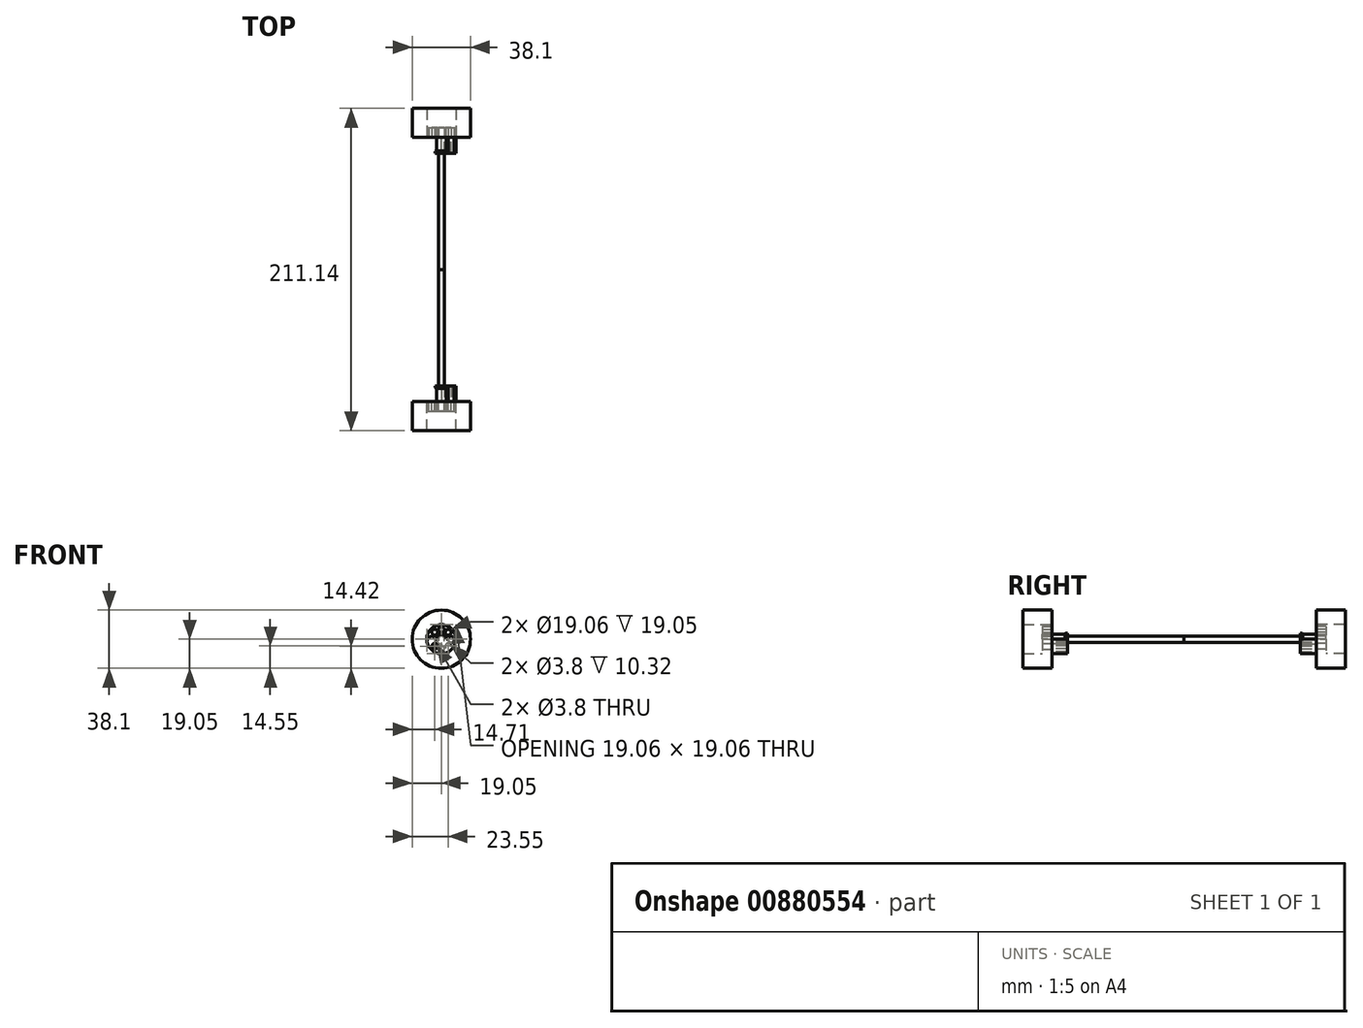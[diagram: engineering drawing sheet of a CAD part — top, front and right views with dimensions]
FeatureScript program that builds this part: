
annotation { "Feature Type Name" : "Feature", "Feature Type Description" : "" }
export const myFeature = defineFeature(function(context is Context, id is Id, definition is map)
    precondition{}
    {
        {
            var Q0;
            Q0=qCreatedBy(makeId("Front.planeOp"),FACE);
            var sketch = newSketch(context, id + "F0", { "sketchPlane" : qUnion([Q0])});
            skCircle(sketch, "E0", {"center": v(0, 0) * mm, "radius": 19.05 * mm});
            skCircle(sketch, "E1", {"center": v(0, 0) * mm, "radius": 9.53 * mm});
            skSolve(sketch);
        }
        {
            var Q0;
            Q0=makeQuery(id+"F0.imprint","IMPRINT",FACE,{"disambiguationData":[TD([[makeQuery(id+"F0.imprint","IMPRINT",EDGE,{"derivedFrom":sQuery(id+"F0.wireOp",EDGE,"E0")}),1.0]])]});
            extrude(context, id + "F1", {"entities" : qUnion([Q0]), "depth" : 19.05 * mm, "offsetDistance" : 25.4 * mm});
        }
        {
            var Q0;
            Q0=makeQuery(id+"F0.imprint","IMPRINT",FACE,{"disambiguationData":[TD([[makeQuery(id+"F0.imprint","IMPRINT",EDGE,{"derivedFrom":sQuery(id+"F0.wireOp",EDGE,"E1")}),1.0]])]});
            extrude(context, id + "F2", {"entities" : qUnion([Q0]), "depth" : 6.35 * mm, "offsetDistance" : 25.4 * mm});
        }
        {
            var Q0;
            Q0=makeQuery(id+"F2.opExtrude","CAP_FACE",FACE,{"disambiguationData":[OSD([sQuery(id+"F0.wireOp",EDGE,"E1")])],"isStart":true});
            var sketch = newSketch(context, id + "F3", { "sketchPlane" : qUnion([Q0])});
            skCircle(sketch, "E2", {"center": v(0, 0) * mm, "radius": 3.18 * mm});
            skLineSegment(sketch, "E3", {"start": v(0, 0) * mm, "end": v(0, 9.53) * mm});
            skLineSegment(sketch, "E4", {"start": v(0, 9.53) * mm, "end": v(0, -9.53) * mm});
            skCircle(sketch, "E5", {"center": v(0, 0) * mm, "radius": 9.53 * mm});
            skLineSegment(sketch, "E6.1.0", {"start": v(9.53, 0) * mm, "end": v(-9.53, 0) * mm});
            skLineSegment(sketch, "E6.2.0", {"start": v(0, -9.53) * mm, "end": v(0, 9.53) * mm});
            skLineSegment(sketch, "E6.anchor1", {"start": v(0, 0) * mm, "end": v(0, -9.53) * mm, "construction": true});
            skLineSegment(sketch, "E6.anchor2", {"start": v(0, 0) * mm, "end": v(0, 9.53) * mm, "construction": true});
            skLineSegment(sketch, "E7", {"start": v(-9.53, 0) * mm, "end": v(-3.18, 0) * mm});
            skCircle(sketch, "E8", {"center": v(-6.35, 0) * mm, "radius": 1.9 * mm});
            skLineSegment(sketch, "E9", {"start": v(0, 0) * mm, "end": v(-6.74, -6.74) * mm});
            skLineSegment(sketch, "E10", {"start": v(-6.74, -6.74) * mm, "end": v(-2.25, -2.25) * mm});
            skCircle(sketch, "E11", {"center": v(-4.5, -4.5) * mm, "radius": 1.9 * mm});
            skLineSegment(sketch, "E12", {"start": v(0, -9.53) * mm, "end": v(0, -3.18) * mm});
            skPoint(sketch, "E12.endSnap0", {"position": v(0, -4.76) * mm});
            skCircle(sketch, "E13", {"center": v(0, -6.35) * mm, "radius": 1.9 * mm});
            skLineSegment(sketch, "E14", {"start": v(2.07, -2.4) * mm, "end": v(6.6, -6.86) * mm});
            skCircle(sketch, "E15", {"center": v(4.34, -4.63) * mm, "radius": 1.9 * mm});
            skLineSegment(sketch, "E16", {"start": v(3.18, 0) * mm, "end": v(9.53, 0) * mm});
            skCircle(sketch, "E17", {"center": v(6.35, 0) * mm, "radius": 1.9 * mm});
            skCircle(sketch, "E18.MirrorC", {"center": v(4.34, 4.63) * mm, "radius": 1.9 * mm});
            skCircle(sketch, "E19.MirrorC", {"center": v(0, 6.35) * mm, "radius": 1.9 * mm});
            skCircle(sketch, "E20.MirrorC", {"center": v(-4.5, 4.5) * mm, "radius": 1.9 * mm});
            skSolve(sketch);
        }
        {
            var Q0;
            Q0=makeQuery(id+"F3.imprint","IMPRINT",FACE,{"disambiguationData":[TD([[makeQuery(id+"F3.imprint","IMPRINT",EDGE,{"derivedFrom":sQuery(id+"F3.wireOp",EDGE,"E2")}),1.0]])]});
            var Q1;
            {var subQ1=sQuery(id+"F3.wireOp",EDGE,"E2");var subQ3=sQuery(id+"F3.wireOp",EDGE,"E6.2.0");var subQ4=makeQuery(id+"F3.imprint","INTERSECT",VERTEX,{"derivedFrom":[subQ1,subQ3]});Q1=makeQuery(id+"F3.imprint","IMPRINT",FACE,{"disambiguationData":[TD([[makeQuery(id+"F3.imprint","IMPRINT",EDGE,{"disambiguationData":[TD([[subQ4,1.0]])],"derivedFrom":subQ1}),1.0]])]});}
            var Q2;
            {var subQ1=sQuery(id+"F3.wireOp",EDGE,"E2");var subQ3=sQuery(id+"F3.wireOp",EDGE,"E6.2.0");var subQ4=makeQuery(id+"F3.imprint","INTERSECT",VERTEX,{"derivedFrom":[subQ1,subQ3]});Q2=makeQuery(id+"F3.imprint","IMPRINT",FACE,{"disambiguationData":[TD([[makeQuery(id+"F3.imprint","IMPRINT",EDGE,{"disambiguationData":[TD([[subQ4,-1.0]])],"derivedFrom":subQ1}),1.0]])]});}
            var Q3;
            {var subQ3=sQuery(id+"F3.wireOp",EDGE,"E9");Q3=makeQuery(id+"F3.imprint","IMPRINT",FACE,{"disambiguationData":[TD([[makeQuery(id+"F3.imprint","IMPRINT",EDGE,{"derivedFrom":subQ3}),1.0]])]});}
            var Q4;
            {var subQ3=sQuery(id+"F3.wireOp",EDGE,"E9");Q4=makeQuery(id+"F3.imprint","IMPRINT",FACE,{"disambiguationData":[TD([[makeQuery(id+"F3.imprint","IMPRINT",EDGE,{"derivedFrom":subQ3}),-1.0]])]});}
            extrude(context, id + "F4", {"entities" : qUnion([Q0, Q1, Q2, Q3, Q4]), "operationType" : NewBodyOperationType.ADD, "depth" : 10.32 * mm, "offsetDistance" : 25.4 * mm});
        }
        {
            var Q0;
            Q0=makeQuery(id+"F3.imprint","IMPRINT",FACE,{"disambiguationData":[TD([[makeQuery(id+"F3.imprint","IMPRINT",EDGE,{"derivedFrom":sQuery(id+"F3.wireOp",EDGE,"E18.MirrorC")}),-1.0]])]});
            var Q1;
            {var subQ0=sQuery(id+"F3.wireOp",EDGE,"E17");var subQ1=sQuery(id+"F3.wireOp",EDGE,"E16");var subQ2=makeQuery(id+"F3.imprint","INTERSECT",VERTEX,{"disambiguationData":[OD(0.0)],"derivedFrom":[subQ1,subQ0]});Q1=makeQuery(id+"F3.imprint","IMPRINT",FACE,{"disambiguationData":[TD([[makeQuery(id+"F3.imprint","IMPRINT",EDGE,{"disambiguationData":[TD([[subQ2,-1.0]])],"derivedFrom":subQ1}),1.0]])]});}
            var Q2;
            {var subQ0=sQuery(id+"F3.wireOp",EDGE,"E17");var subQ1=sQuery(id+"F3.wireOp",EDGE,"E16");var subQ2=makeQuery(id+"F3.imprint","INTERSECT",VERTEX,{"disambiguationData":[OD(0.0)],"derivedFrom":[subQ1,subQ0]});Q2=makeQuery(id+"F3.imprint","IMPRINT",FACE,{"disambiguationData":[TD([[makeQuery(id+"F3.imprint","IMPRINT",EDGE,{"disambiguationData":[TD([[subQ2,-1.0]])],"derivedFrom":subQ1}),-1.0]])]});}
            var Q3;
            {var subQ0=sQuery(id+"F3.wireOp",EDGE,"E15");var subQ1=sQuery(id+"F3.wireOp",EDGE,"E14");var subQ2=makeQuery(id+"F3.imprint","INTERSECT",VERTEX,{"disambiguationData":[OD(0.0)],"derivedFrom":[subQ1,subQ0]});Q3=makeQuery(id+"F3.imprint","IMPRINT",FACE,{"disambiguationData":[TD([[makeQuery(id+"F3.imprint","IMPRINT",EDGE,{"disambiguationData":[TD([[subQ2,-1.0]])],"derivedFrom":subQ1}),1.0]])]});}
            var Q4;
            {var subQ0=sQuery(id+"F3.wireOp",EDGE,"E15");var subQ1=sQuery(id+"F3.wireOp",EDGE,"E14");var subQ2=makeQuery(id+"F3.imprint","INTERSECT",VERTEX,{"disambiguationData":[OD(0.0)],"derivedFrom":[subQ1,subQ0]});Q4=makeQuery(id+"F3.imprint","IMPRINT",FACE,{"disambiguationData":[TD([[makeQuery(id+"F3.imprint","IMPRINT",EDGE,{"disambiguationData":[TD([[subQ2,-1.0]])],"derivedFrom":subQ1}),-1.0]])]});}
            var Q5;
            {var subQ0=sQuery(id+"F3.wireOp",EDGE,"E13");var subQ1=sQuery(id+"F3.wireOp",EDGE,"E12");var subQ2=makeQuery(id+"F3.imprint","INTERSECT",VERTEX,{"disambiguationData":[OD(0.0)],"derivedFrom":[subQ1,subQ0]});Q5=makeQuery(id+"F3.imprint","IMPRINT",FACE,{"disambiguationData":[TD([[makeQuery(id+"F3.imprint","IMPRINT",EDGE,{"disambiguationData":[TD([[subQ2,-1.0]])],"derivedFrom":subQ1}),-1.0]])]});}
            var Q6;
            {var subQ0=sQuery(id+"F3.wireOp",EDGE,"E13");var subQ1=sQuery(id+"F3.wireOp",EDGE,"E12");var subQ2=makeQuery(id+"F3.imprint","INTERSECT",VERTEX,{"disambiguationData":[OD(0.0)],"derivedFrom":[subQ1,subQ0]});Q6=makeQuery(id+"F3.imprint","IMPRINT",FACE,{"disambiguationData":[TD([[makeQuery(id+"F3.imprint","IMPRINT",EDGE,{"disambiguationData":[TD([[subQ2,-1.0]])],"derivedFrom":subQ1}),1.0]])]});}
            var Q7;
            {var subQ0=sQuery(id+"F3.wireOp",EDGE,"E11");var subQ1=sQuery(id+"F3.wireOp",EDGE,"E10");var subQ2=makeQuery(id+"F3.imprint","INTERSECT",VERTEX,{"disambiguationData":[OD(0.0)],"derivedFrom":[subQ1,subQ0]});Q7=makeQuery(id+"F3.imprint","IMPRINT",FACE,{"disambiguationData":[TD([[makeQuery(id+"F3.imprint","IMPRINT",EDGE,{"disambiguationData":[TD([[subQ2,-1.0]])],"derivedFrom":subQ1}),-1.0]])]});}
            var Q8;
            {var subQ0=sQuery(id+"F3.wireOp",EDGE,"E11");var subQ1=sQuery(id+"F3.wireOp",EDGE,"E10");var subQ2=makeQuery(id+"F3.imprint","INTERSECT",VERTEX,{"disambiguationData":[OD(0.0)],"derivedFrom":[subQ1,subQ0]});Q8=makeQuery(id+"F3.imprint","IMPRINT",FACE,{"disambiguationData":[TD([[makeQuery(id+"F3.imprint","IMPRINT",EDGE,{"disambiguationData":[TD([[subQ2,-1.0]])],"derivedFrom":subQ1}),1.0]])]});}
            var Q9;
            {var subQ0=sQuery(id+"F3.wireOp",EDGE,"E8");var subQ1=sQuery(id+"F3.wireOp",EDGE,"E7");var subQ2=makeQuery(id+"F3.imprint","INTERSECT",VERTEX,{"disambiguationData":[OD(0.0)],"derivedFrom":[subQ1,subQ0]});Q9=makeQuery(id+"F3.imprint","IMPRINT",FACE,{"disambiguationData":[TD([[makeQuery(id+"F3.imprint","IMPRINT",EDGE,{"disambiguationData":[TD([[subQ2,-1.0]])],"derivedFrom":subQ1}),-1.0]])]});}
            var Q10;
            {var subQ0=sQuery(id+"F3.wireOp",EDGE,"E8");var subQ1=sQuery(id+"F3.wireOp",EDGE,"E7");var subQ2=makeQuery(id+"F3.imprint","INTERSECT",VERTEX,{"disambiguationData":[OD(0.0)],"derivedFrom":[subQ1,subQ0]});Q10=makeQuery(id+"F3.imprint","IMPRINT",FACE,{"disambiguationData":[TD([[makeQuery(id+"F3.imprint","IMPRINT",EDGE,{"disambiguationData":[TD([[subQ2,-1.0]])],"derivedFrom":subQ1}),1.0]])]});}
            var Q11;
            Q11=makeQuery(id+"F3.imprint","IMPRINT",FACE,{"disambiguationData":[TD([[makeQuery(id+"F3.imprint","IMPRINT",EDGE,{"derivedFrom":sQuery(id+"F3.wireOp",EDGE,"E20.MirrorC")}),-1.0]])]});
            var Q12;
            {var subQ0=sQuery(id+"F3.wireOp",EDGE,"E19.MirrorC");var subQ1=sQuery(id+"F3.wireOp",EDGE,"E6.2.0");var subQ2=makeQuery(id+"F3.imprint","INTERSECT",VERTEX,{"disambiguationData":[OD(0.0)],"derivedFrom":[subQ1,subQ0]});Q12=makeQuery(id+"F3.imprint","IMPRINT",FACE,{"disambiguationData":[TD([[makeQuery(id+"F3.imprint","IMPRINT",EDGE,{"disambiguationData":[TD([[subQ2,-1.0]])],"derivedFrom":subQ1}),1.0]])]});}
            var Q13;
            {var subQ0=sQuery(id+"F3.wireOp",EDGE,"E19.MirrorC");var subQ1=sQuery(id+"F3.wireOp",EDGE,"E6.2.0");var subQ2=makeQuery(id+"F3.imprint","INTERSECT",VERTEX,{"disambiguationData":[OD(0.0)],"derivedFrom":[subQ1,subQ0]});Q13=makeQuery(id+"F3.imprint","IMPRINT",FACE,{"disambiguationData":[TD([[makeQuery(id+"F3.imprint","IMPRINT",EDGE,{"disambiguationData":[TD([[subQ2,-1.0]])],"derivedFrom":subQ1}),-1.0]])]});}
            extrude(context, id + "F5", {"entities" : qUnion([Q0, Q1, Q2, Q3, Q4, Q5, Q6, Q7, Q8, Q9, Q10, Q11, Q12, Q13]), "operationType" : NewBodyOperationType.REMOVE, "oppositeDirection" : true, "depth" : 6.35 * mm, "offsetDistance" : 25.4 * mm});
        }
        {
            var Q0;
            Q0=makeQuery(id+"F4.opExtrude","CAP_FACE",FACE,{"disambiguationData":[OSD([sQuery(id+"F3.wireOp",EDGE,"E2")])],"isStart":false});
            var sketch = newSketch(context, id + "F6", { "sketchPlane" : qUnion([Q0])});
            skCircle(sketch, "E21", {"center": v(0, 0) * mm, "radius": 3.97 * mm});
            skCircle(sketch, "E22", {"center": v(0, 0) * mm, "radius": 1.98 * mm});
            skSolve(sketch);
        }
        {
            var Q0;
            Q0=makeQuery(id+"F6.imprint","IMPRINT",FACE,{"disambiguationData":[TD([[makeQuery(id+"F6.imprint","IMPRINT",EDGE,{"derivedFrom":sQuery(id+"F6.wireOp",EDGE,"E21")}),1.0]])]});
            extrude(context, id + "F7", {"entities" : qUnion([Q0]), "operationType" : NewBodyOperationType.ADD, "oppositeDirection" : true, "depth" : 1.59 * mm, "offsetDistance" : 25.4 * mm});
        }
        {
            var Q0;
            Q0=makeQuery(id+"F7.opExtrude","CAP_EDGE",EDGE,{"disambiguationData":[OSD([sQuery(id+"F6.wireOp",EDGE,"E21")])],"isStart":false});
            chamfer(context, id + "F8", {"entities" : qUnion([Q0]), "width" : 0.5 * mm, "tangentPropagation" : true});
        }
        {
            var Q0;
            Q0=makeQuery(id+"F6.imprint","IMPRINT",FACE,{"disambiguationData":[TD([[makeQuery(id+"F6.imprint","IMPRINT",EDGE,{"derivedFrom":sQuery(id+"F6.wireOp",EDGE,"E22")}),1.0]])]});
            extrude(context, id + "F9", {"entities" : qUnion([Q0]), "operationType" : NewBodyOperationType.ADD, "depth" : 76.2 * mm, "offsetDistance" : 25.4 * mm});
        }
        {
            var Q0;
            Q0=makeQuery(id+"F1.opExtrude","SWEPT_BODY",BODY,{"disambiguationData":[OSD([sQuery(id+"F0.wireOp",EDGE,"E0"),sQuery(id+"F0.wireOp",EDGE,"E1")])]});
            var Q1;
            Q1=makeQuery(id+"F2.opExtrude","SWEPT_BODY",BODY,{"disambiguationData":[OSD([sQuery(id+"F0.wireOp",EDGE,"E1")])]});
            var Q2;
            Q2=makeQuery(id+"F7.opExtrude","SWEPT_BODY",BODY,{"disambiguationData":[OSD([sQuery(id+"F3.wireOp",EDGE,"E2"),sQuery(id+"F6.wireOp",EDGE,"E21")])]});
            var Q3;
            Q3=makeQuery(id+"F9.opExtrude","CAP_FACE",FACE,{"disambiguationData":[OSD([sQuery(id+"F6.wireOp",EDGE,"E22")])],"isStart":false});
            mirror(context, id + "F10", {"entities" : qUnion([Q0, Q1, Q2]), "mirrorPlane" : qUnion([Q3])});
        }
    });
